# Revit family: Basin-Countertop-American_Standard-Studio-0642_Series
name_source: partatom
category: Plumbing Fixtures
units: mm (PartAtom-declared; Revit-internal decimal feet)

## family parameters
Always vertical = No
Cut with Voids When Loaded = Yes
OmniClass Number = 23.45.05.14.14
OmniClass Title = Sinks/Lavatories
Part Type = Normal
Room Calculation Point = No
Round Connector Dimension = Use Radius
Shared = Yes
Work Plane-Based = Yes

## types (2) — shared parameters
ADA Compliant = Yes
Assembly Code = D2010310
Basin Shape = Oval
CW Connection = Yes
CWFU = 1.5
Cold Water Connection Diameter = 1/2"
Cold Water Connection Height = 21 1/4"
Cold Water Connection Radius = 1/4"
Cold Water Connection Width = 4"
Default Elevation = 34"
Finish = Vitreous China-American Standard-020-White
Finished Wall to Basin = 2"
Finished Wall to Basin Constraint = 2"
HW Connection = Yes
HWFU = 1.5
Height = 6 3/4"
Hot Water Connection Diameter = 1/2"
Hot Water Connection Height = 21 1/4"
Hot Water Connection Radius = 1/4"
Hot Water Connection Width = 4"
Installation Type = Countertop
Length = 16 1/4"
Manufacturer = American Standard
Material = Vitreous China-American Standard-020-White
Price = Prices may vary. Please consult Manufacturer Representative for most up-to-date price list.
Product Documentation Link = https://americanstandard.box.com
Product Page URL = https://www.americanstandard.ca
Revised Date = 02/17/2022
URL = https://www.americanstandard.ca
Vent Connection = No
WFU = 2
Waste Connection = Yes
Waste Connection Diameter = 1 1/4"
Waste Connection Height = 19 1/2"
Waste Connection Radius = 5/8"
Width = 16 1/4"

## per-type parameters (varying)
| type | Description | Hole Punch Location |
| 0642.008.020 | Studio Carré Countertop Sink. 8" centers. | 8" |
| 0642.001.020 | Studio Carré Countertop Sink. Center hole only. | 24" |

note: column(s) folded — value = type name in every type: Model

## geometry (parser evidence)
native form markers: Sweep x2
no freeform markers — native parametric forms only
